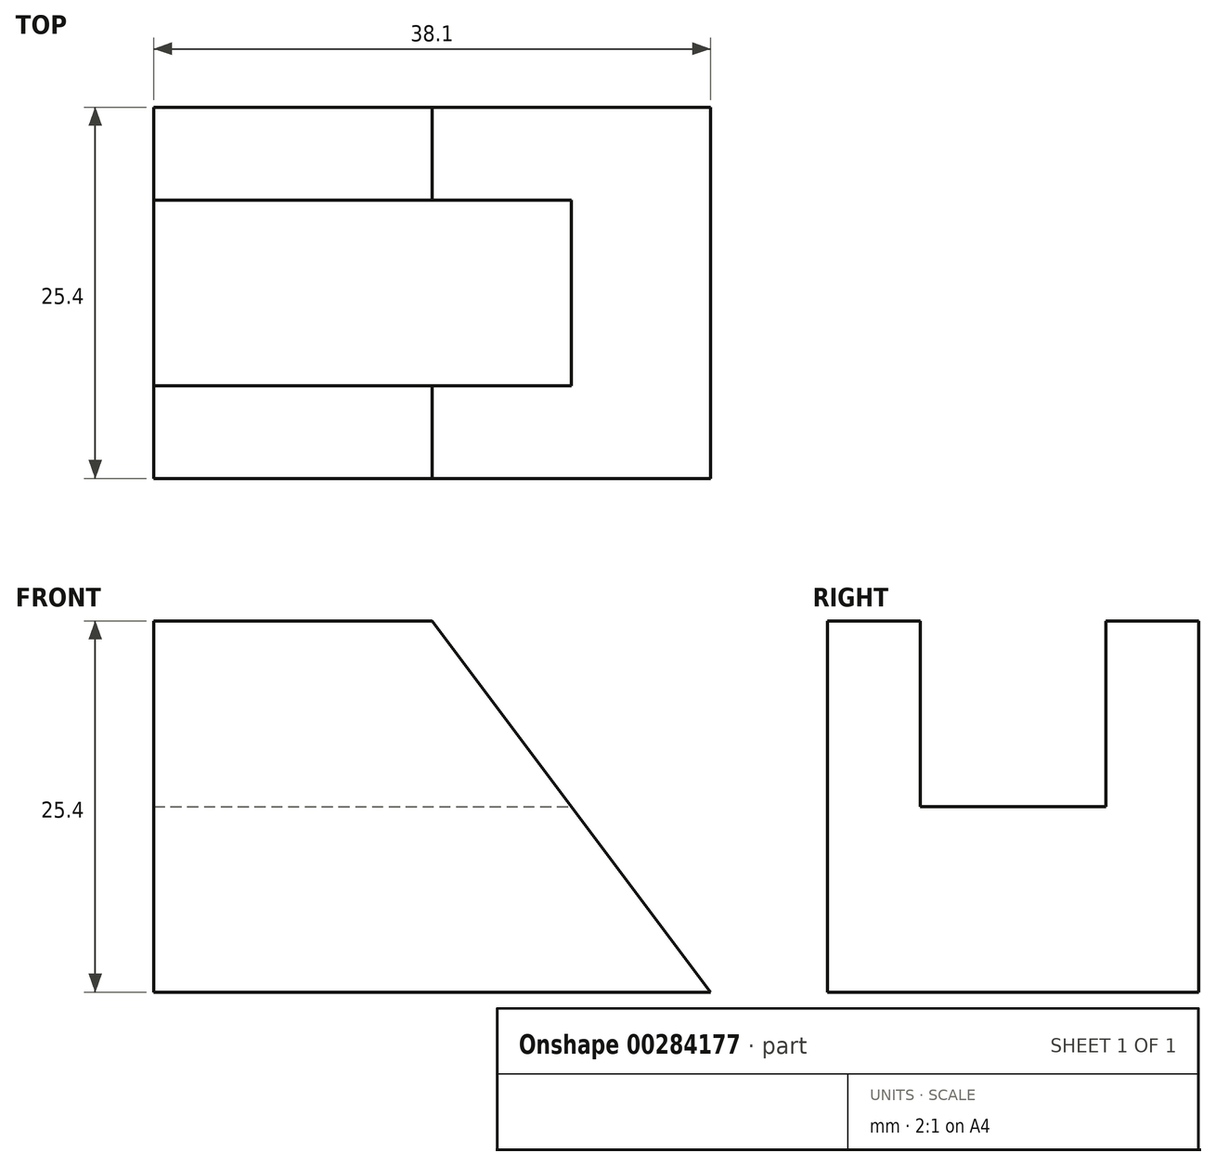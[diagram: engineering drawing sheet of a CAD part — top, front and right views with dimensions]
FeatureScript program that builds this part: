
annotation { "Feature Type Name" : "Feature", "Feature Type Description" : "" }
export const myFeature = defineFeature(function(context is Context, id is Id, definition is map)
    precondition{}
    {
        {
            var Q0;
            Q0=qCreatedBy(makeId("Top.planeOp"),FACE);
            var sketch = newSketch(context, id + "F0", { "sketchPlane" : qUnion([Q0])});
            skLineSegment(sketch, "E0.bottom", {"start": v(0, 25.4) * mm, "end": v(38.1, 25.4) * mm});
            skLineSegment(sketch, "E0.top", {"start": v(0, 0) * mm, "end": v(38.1, 0) * mm});
            skLineSegment(sketch, "E0.left", {"start": v(0, 25.4) * mm, "end": v(0, 0) * mm});
            skLineSegment(sketch, "E0.right", {"start": v(38.1, 25.4) * mm, "end": v(38.1, 0) * mm});
            skSolve(sketch);
        }
        {
            var Q0;
            Q0=makeQuery(id+"F0.imprint","IMPRINT",FACE,{"disambiguationData":[TD([[makeQuery(id+"F0.imprint","IMPRINT",EDGE,{"derivedFrom":sQuery(id+"F0.wireOp",EDGE,"E0.bottom")}),-1.0]])]});
            extrude(context, id + "F1", {"entities" : qUnion([Q0]), "oppositeDirection" : true, "depth" : 25.4 * mm});
        }
        {
            var Q0;
            Q0=qCreatedBy(makeId("Top.planeOp"),FACE);
            var sketch = newSketch(context, id + "F2", { "sketchPlane" : qUnion([Q0])});
            skLineSegment(sketch, "E1.bottom", {"start": v(0, 19.05) * mm, "end": v(28.58, 19.05) * mm});
            skLineSegment(sketch, "E1.top", {"start": v(0, 6.35) * mm, "end": v(28.58, 6.35) * mm});
            skLineSegment(sketch, "E1.left", {"start": v(0, 19.05) * mm, "end": v(0, 6.35) * mm});
            skLineSegment(sketch, "E1.right", {"start": v(28.58, 19.05) * mm, "end": v(28.58, 6.35) * mm});
            skSolve(sketch);
        }
        {
            var Q0;
            Q0=makeQuery(id+"F2.imprint","IMPRINT",FACE,{"disambiguationData":[TD([[makeQuery(id+"F2.imprint","IMPRINT",EDGE,{"derivedFrom":sQuery(id+"F2.wireOp",EDGE,"E1.bottom")}),-1.0]])]});
            extrude(context, id + "F3", {"entities" : qUnion([Q0]), "operationType" : NewBodyOperationType.REMOVE, "oppositeDirection" : true, "depth" : 12.7 * mm});
        }
        {
            var Q0;
            Q0=qCreatedBy(makeId("Front.planeOp"),FACE);
            var sketch = newSketch(context, id + "F4", { "sketchPlane" : qUnion([Q0])});
            skLineSegment(sketch, "E2", {"start": v(38.1, 0) * mm, "end": v(38.1, -25.4) * mm});
            skLineSegment(sketch, "E3", {"start": v(38.1, -25.4) * mm, "end": v(19.05, 0) * mm});
            skLineSegment(sketch, "E4", {"start": v(19.05, 0) * mm, "end": v(38.1, 0) * mm});
            skSolve(sketch);
        }
        {
            var Q0;
            Q0 = qSketchRegion(id + "F4", true);
            extrude(context, id + "F5", {"entities" : qUnion([Q0]), "operationType" : NewBodyOperationType.REMOVE, "oppositeDirection" : true, "depth" : 25.4 * mm});
        }
    });
